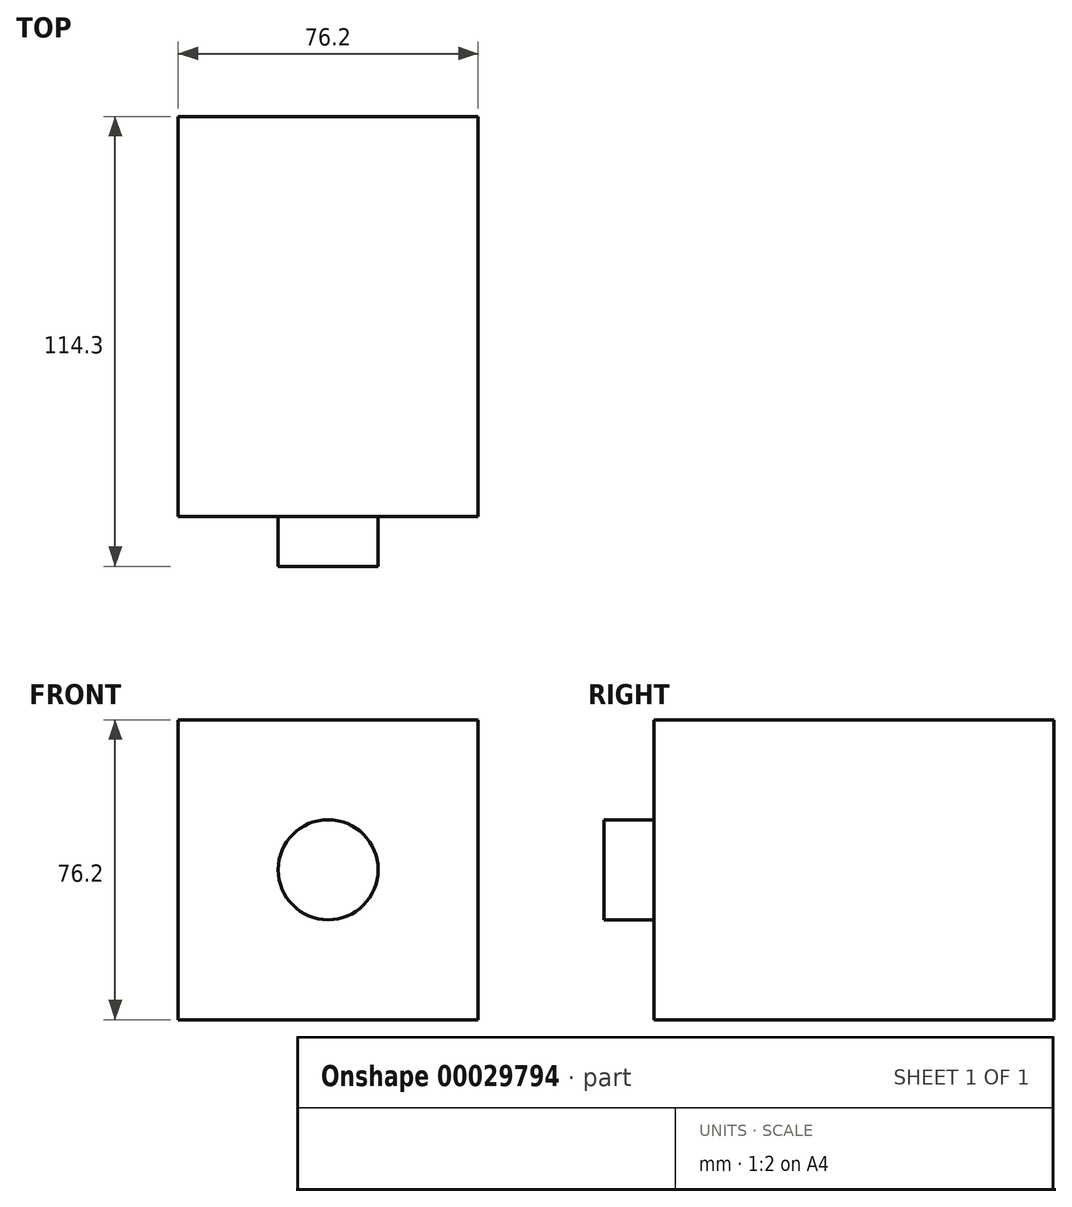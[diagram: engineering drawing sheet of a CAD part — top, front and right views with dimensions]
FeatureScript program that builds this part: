
annotation { "Feature Type Name" : "Feature", "Feature Type Description" : "" }
export const myFeature = defineFeature(function(context is Context, id is Id, definition is map)
    precondition{}
    {
        {
            var Q0;
            Q0=qCreatedBy(makeId("Front.planeOp"),FACE);
            var sketch = newSketch(context, id + "F0", { "sketchPlane" : qUnion([Q0])});
            skLineSegment(sketch, "E0.rect.bottom", {"start": v(38.1, 38.1) * mm, "end": v(-38.1, 38.1) * mm});
            skLineSegment(sketch, "E0.rect.top", {"start": v(38.1, -38.1) * mm, "end": v(-38.1, -38.1) * mm});
            skLineSegment(sketch, "E0.rect.left", {"start": v(38.1, 38.1) * mm, "end": v(38.1, -38.1) * mm});
            skLineSegment(sketch, "E0.rect.right", {"start": v(-38.1, 38.1) * mm, "end": v(-38.1, -38.1) * mm});
            skPoint(sketch, "E0.rect.middle", {"position": v(0, 0) * mm});
            skCircle(sketch, "E1", {"center": v(0, 0) * mm, "radius": 12.7 * mm});
            skLineSegment(sketch, "E2", {"start": v(0, 0) * mm, "end": v(0, 12.7) * mm});
            skSolve(sketch);
        }
        {
            var Q0;
            Q0=makeQuery(id+"F0.imprint","IMPRINT",FACE,{"disambiguationData":[TD([[makeQuery(id+"F0.imprint","IMPRINT",EDGE,{"derivedFrom":sQuery(id+"F0.wireOp",EDGE,"E0.rect.bottom")}),1.0]])]});
            extrude(context, id + "F1", {"entities" : qUnion([Q0]), "depth" : 101.6 * mm});
        }
        {
            var Q0;
            Q0=makeQuery(id+"F0.imprint","IMPRINT",FACE,{"disambiguationData":[TD([[makeQuery(id+"F0.imprint","IMPRINT",EDGE,{"derivedFrom":sQuery(id+"F0.wireOp",EDGE,"E1")}),1.0]])]});
            extrude(context, id + "F2", {"entities" : qUnion([Q0]), "operationType" : NewBodyOperationType.ADD, "depth" : 114.3 * mm});
        }
    });
